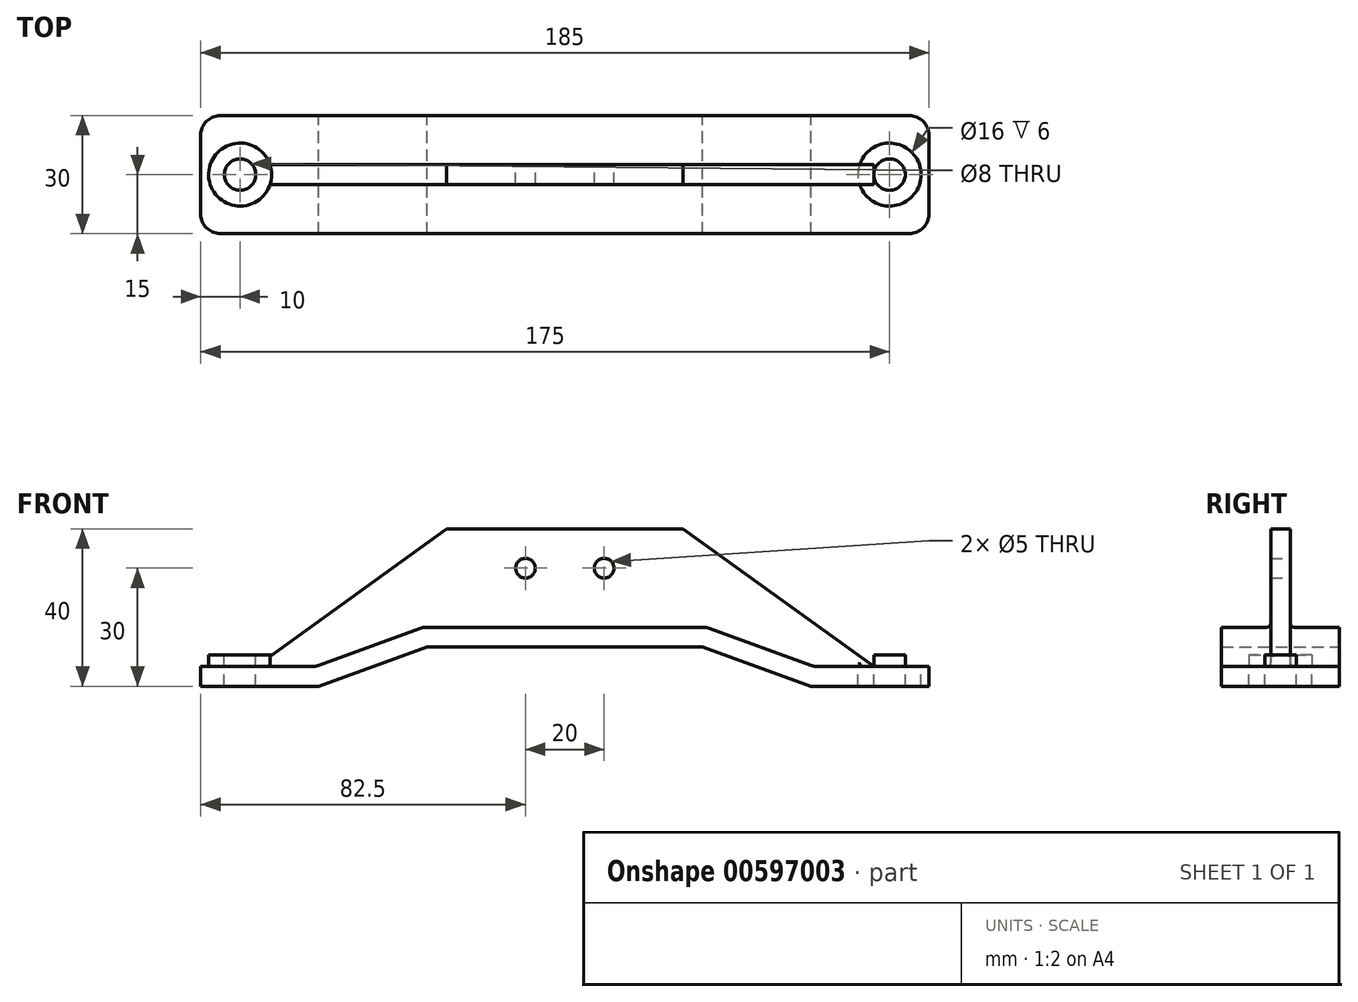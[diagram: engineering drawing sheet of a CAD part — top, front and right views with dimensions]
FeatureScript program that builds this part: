
annotation { "Feature Type Name" : "Feature", "Feature Type Description" : "" }
export const myFeature = defineFeature(function(context is Context, id is Id, definition is map)
    precondition{}
    {
        {
            var Q0;
            Q0=qCreatedBy(makeId("Front.planeOp"),FACE);
            var sketch = newSketch(context, id + "F0", { "sketchPlane" : qUnion([Q0])});
            skLineSegment(sketch, "E0", {"start": v(0, 0) * mm, "end": v(-35.03, 0) * mm});
            skLineSegment(sketch, "E1", {"start": v(-35.03, 0) * mm, "end": v(-62.5, -10) * mm});
            skLineSegment(sketch, "E2", {"start": v(-62.5, -10) * mm, "end": v(-92.5, -10) * mm});
            skLineSegment(sketch, "E3.MirrorCS", {"start": v(0, 0) * mm, "end": v(35.03, 0) * mm});
            skLineSegment(sketch, "E4.MirrorCS", {"start": v(35.03, 0) * mm, "end": v(62.5, -10) * mm});
            skLineSegment(sketch, "E5.MirrorCS", {"start": v(62.5, -10) * mm, "end": v(92.5, -10) * mm});
            skLineSegment(sketch, "E6", {"start": v(-62.5, -10) * mm, "end": v(0, -10) * mm, "construction": true});
            skLineSegment(sketch, "E7.0", {"start": v(-63.38, -5) * mm, "end": v(-92.5, -5) * mm});
            skLineSegment(sketch, "E7.1", {"start": v(-35.9, 5) * mm, "end": v(-63.38, -5) * mm});
            skLineSegment(sketch, "E7.2", {"start": v(63.38, -5) * mm, "end": v(92.5, -5) * mm});
            skLineSegment(sketch, "E7.3", {"start": v(35.9, 5) * mm, "end": v(63.38, -5) * mm});
            skLineSegment(sketch, "E7.4", {"start": v(0, 5) * mm, "end": v(35.9, 5) * mm});
            skLineSegment(sketch, "E7.5", {"start": v(0, 5) * mm, "end": v(-35.9, 5) * mm});
            skLineSegment(sketch, "E8", {"start": v(-92.5, -5) * mm, "end": v(-92.5, -10) * mm});
            skLineSegment(sketch, "E9", {"start": v(92.5, -5) * mm, "end": v(92.5, -10) * mm});
            skLineSegment(sketch, "E10", {"start": v(-78.5, -5) * mm, "end": v(-30, 30) * mm});
            skLineSegment(sketch, "E11", {"start": v(-30, 30) * mm, "end": v(0, 30) * mm});
            skLineSegment(sketch, "E12.MirrorCS", {"start": v(30, 30) * mm, "end": v(0, 30) * mm});
            skLineSegment(sketch, "E13.MirrorCS", {"start": v(78.5, -5) * mm, "end": v(30, 30) * mm});
            skCircle(sketch, "E14", {"center": v(-10, 20) * mm, "radius": 2.5 * mm});
            skCircle(sketch, "E15.MirrorC", {"center": v(10, 20) * mm, "radius": 2.5 * mm});
            skSolve(sketch);
        }
        {
            var Q0;
            Q0=makeQuery(id+"F0.imprint","IMPRINT",FACE,{"disambiguationData":[TD([[makeQuery(id+"F0.imprint","IMPRINT",EDGE,{"derivedFrom":sQuery(id+"F0.wireOp",EDGE,"E0")}),-1.0]])]});
            extrude(context, id + "F1", {"entities" : qUnion([Q0]), "endBound" : BoundingType.SYMMETRIC, "depth" : 30 * mm, "offsetDistance" : 25 * mm});
        }
        {
            var Q0;
            Q0=makeQuery(id+"F1.opExtrude","SWEPT_FACE",FACE,{"disambiguationData":[OSD([sQuery(id+"F0.wireOp",EDGE,"E7.0")])]});
            var sketch = newSketch(context, id + "F2", { "sketchPlane" : qUnion([Q0])});
            skCircle(sketch, "E16", {"center": v(-82.5, 0) * mm, "radius": 4 * mm});
            skLineSegment(sketch, "E17", {"start": v(-92.5, 0) * mm, "end": v(-82.5, 0) * mm, "construction": true});
            skPoint(sketch, "E17.endSnap0", {"position": v(-92.5, 0) * mm});
            skCircle(sketch, "E18.MirrorC", {"center": v(82.5, 0) * mm, "radius": 4 * mm});
            skCircle(sketch, "E19.0", {"center": v(-82.5, 0) * mm, "radius": 8 * mm});
            skCircle(sketch, "E20.MirrorC", {"center": v(82.5, 0) * mm, "radius": 8 * mm});
            skSolve(sketch);
        }
        {
            var Q0;
            Q0 = qSketchRegion(id + "F0", true);
            extrude(context, id + "F3", {"entities" : qUnion([Q0]), "operationType" : NewBodyOperationType.ADD, "endBound" : BoundingType.SYMMETRIC, "depth" : 5 * mm, "offsetDistance" : 25 * mm});
        }
        {
            var Q0;
            Q0=makeQuery(id+"F2.imprint","IMPRINT",FACE,{"disambiguationData":[TD([[makeQuery(id+"F2.imprint","IMPRINT",EDGE,{"derivedFrom":sQuery(id+"F2.wireOp",EDGE,"E16")}),1.0]])]});
            var Q1;
            Q1=makeQuery(id+"F2.imprint","IMPRINT",FACE,{"disambiguationData":[TD([[makeQuery(id+"F2.imprint","IMPRINT",EDGE,{"derivedFrom":sQuery(id+"F2.wireOp",EDGE,"E18.MirrorC")}),-1.0]])]});
            extrude(context, id + "F4", {"entities" : qUnion([Q0, Q1]), "operationType" : NewBodyOperationType.REMOVE, "endBound" : BoundingType.THROUGH_ALL, "oppositeDirection" : true, "depth" : 25 * mm, "offsetDistance" : 25 * mm});
        }
        {
            var Q0;
            {var subQ0=sQuery(id+"F0.wireOp",EDGE,"E9");var subQ1=sQuery(id+"F0.wireOp",EDGE,"E8");var subQ2=sQuery(id+"F0.wireOp",EDGE,"E7.2");var subQ3=sQuery(id+"F0.wireOp",EDGE,"E7.1");var subQ4=sQuery(id+"F0.wireOp",EDGE,"E7.0");var subQ5=sQuery(id+"F0.wireOp",EDGE,"E5.MirrorCS");var subQ6=sQuery(id+"F0.wireOp",EDGE,"E4.MirrorCS");var subQ7=sQuery(id+"F0.wireOp",EDGE,"E3.MirrorCS");var subQ8=sQuery(id+"F0.wireOp",EDGE,"E2");var subQ9=sQuery(id+"F0.wireOp",EDGE,"E1");var subQ10=sQuery(id+"F0.wireOp",EDGE,"E0");Q0=makeQuery(id+"F3.boolean.opBoolean","SPLIT",EDGE,{"disambiguationData":[TD([makeQuery(id+"F1.opExtrude","CAP_FACE",FACE,{"disambiguationData":[OSD([subQ10,subQ9,subQ8,subQ7,subQ6,subQ5,subQ4,subQ3,subQ2,sQuery(id+"F0.wireOp",EDGE,"E7.3"),sQuery(id+"F0.wireOp",EDGE,"E7.4"),sQuery(id+"F0.wireOp",EDGE,"E7.5"),subQ1,subQ0])],"isStart":false})])],"derivedFrom":makeQuery(id+"F1.opExtrude","SWEPT_EDGE",EDGE,{"disambiguationData":[OSD([subQ4,subQ3])]})});}
            var Q1;
            {var subQ0=sQuery(id+"F0.wireOp",EDGE,"E9");var subQ1=sQuery(id+"F0.wireOp",EDGE,"E8");var subQ2=sQuery(id+"F0.wireOp",EDGE,"E7.2");var subQ3=sQuery(id+"F0.wireOp",EDGE,"E7.1");var subQ4=sQuery(id+"F0.wireOp",EDGE,"E7.0");var subQ5=sQuery(id+"F0.wireOp",EDGE,"E5.MirrorCS");var subQ6=sQuery(id+"F0.wireOp",EDGE,"E4.MirrorCS");var subQ7=sQuery(id+"F0.wireOp",EDGE,"E3.MirrorCS");var subQ8=sQuery(id+"F0.wireOp",EDGE,"E2");var subQ9=sQuery(id+"F0.wireOp",EDGE,"E1");var subQ10=sQuery(id+"F0.wireOp",EDGE,"E0");Q1=makeQuery(id+"F3.boolean.opBoolean","SPLIT",EDGE,{"disambiguationData":[TD([makeQuery(id+"F1.opExtrude","CAP_FACE",FACE,{"disambiguationData":[OSD([subQ10,subQ9,subQ8,subQ7,subQ6,subQ5,subQ4,subQ3,subQ2,sQuery(id+"F0.wireOp",EDGE,"E7.3"),sQuery(id+"F0.wireOp",EDGE,"E7.4"),sQuery(id+"F0.wireOp",EDGE,"E7.5"),subQ1,subQ0])],"isStart":true})])],"derivedFrom":makeQuery(id+"F1.opExtrude","SWEPT_EDGE",EDGE,{"disambiguationData":[OSD([subQ4,subQ3])]})});}
            var Q2;
            {var subQ0=sQuery(id+"F0.wireOp",EDGE,"E9");var subQ1=sQuery(id+"F0.wireOp",EDGE,"E8");var subQ2=sQuery(id+"F0.wireOp",EDGE,"E7.5");var subQ3=sQuery(id+"F0.wireOp",EDGE,"E7.4");var subQ4=sQuery(id+"F0.wireOp",EDGE,"E7.2");var subQ5=sQuery(id+"F0.wireOp",EDGE,"E7.1");var subQ6=sQuery(id+"F0.wireOp",EDGE,"E7.0");var subQ7=sQuery(id+"F0.wireOp",EDGE,"E5.MirrorCS");var subQ8=sQuery(id+"F0.wireOp",EDGE,"E4.MirrorCS");var subQ9=sQuery(id+"F0.wireOp",EDGE,"E3.MirrorCS");var subQ10=sQuery(id+"F0.wireOp",EDGE,"E2");var subQ11=sQuery(id+"F0.wireOp",EDGE,"E1");var subQ12=sQuery(id+"F0.wireOp",EDGE,"E0");Q2=makeQuery(id+"F3.boolean.opBoolean","SPLIT",EDGE,{"disambiguationData":[TD([makeQuery(id+"F1.opExtrude","CAP_FACE",FACE,{"disambiguationData":[OSD([subQ12,subQ11,subQ10,subQ9,subQ8,subQ7,subQ6,subQ5,subQ4,sQuery(id+"F0.wireOp",EDGE,"E7.3"),subQ3,subQ2,subQ1,subQ0])],"isStart":false})])],"derivedFrom":makeQuery(id+"F1.opExtrude","SWEPT_EDGE",EDGE,{"disambiguationData":[OSD([subQ5,subQ2])]})});}
            var Q3;
            {var subQ0=sQuery(id+"F0.wireOp",EDGE,"E9");var subQ1=sQuery(id+"F0.wireOp",EDGE,"E8");var subQ2=sQuery(id+"F0.wireOp",EDGE,"E7.5");var subQ3=sQuery(id+"F0.wireOp",EDGE,"E7.4");var subQ4=sQuery(id+"F0.wireOp",EDGE,"E7.2");var subQ5=sQuery(id+"F0.wireOp",EDGE,"E7.1");var subQ6=sQuery(id+"F0.wireOp",EDGE,"E7.0");var subQ7=sQuery(id+"F0.wireOp",EDGE,"E5.MirrorCS");var subQ8=sQuery(id+"F0.wireOp",EDGE,"E4.MirrorCS");var subQ9=sQuery(id+"F0.wireOp",EDGE,"E3.MirrorCS");var subQ10=sQuery(id+"F0.wireOp",EDGE,"E2");var subQ11=sQuery(id+"F0.wireOp",EDGE,"E1");var subQ12=sQuery(id+"F0.wireOp",EDGE,"E0");Q3=makeQuery(id+"F3.boolean.opBoolean","SPLIT",EDGE,{"disambiguationData":[TD([makeQuery(id+"F1.opExtrude","CAP_FACE",FACE,{"disambiguationData":[OSD([subQ12,subQ11,subQ10,subQ9,subQ8,subQ7,subQ6,subQ5,subQ4,sQuery(id+"F0.wireOp",EDGE,"E7.3"),subQ3,subQ2,subQ1,subQ0])],"isStart":true})])],"derivedFrom":makeQuery(id+"F1.opExtrude","SWEPT_EDGE",EDGE,{"disambiguationData":[OSD([subQ5,subQ2])]})});}
            var Q4;
            {var subQ0=sQuery(id+"F0.wireOp",EDGE,"E9");var subQ1=sQuery(id+"F0.wireOp",EDGE,"E8");var subQ2=sQuery(id+"F0.wireOp",EDGE,"E7.3");var subQ3=sQuery(id+"F0.wireOp",EDGE,"E7.2");var subQ4=sQuery(id+"F0.wireOp",EDGE,"E7.0");var subQ5=sQuery(id+"F0.wireOp",EDGE,"E5.MirrorCS");var subQ6=sQuery(id+"F0.wireOp",EDGE,"E4.MirrorCS");var subQ7=sQuery(id+"F0.wireOp",EDGE,"E3.MirrorCS");var subQ8=sQuery(id+"F0.wireOp",EDGE,"E2");var subQ9=sQuery(id+"F0.wireOp",EDGE,"E1");var subQ10=sQuery(id+"F0.wireOp",EDGE,"E0");Q4=makeQuery(id+"F3.boolean.opBoolean","SPLIT",EDGE,{"disambiguationData":[TD([makeQuery(id+"F1.opExtrude","CAP_FACE",FACE,{"disambiguationData":[OSD([subQ10,subQ9,subQ8,subQ7,subQ6,subQ5,subQ4,sQuery(id+"F0.wireOp",EDGE,"E7.1"),subQ3,subQ2,sQuery(id+"F0.wireOp",EDGE,"E7.4"),sQuery(id+"F0.wireOp",EDGE,"E7.5"),subQ1,subQ0])],"isStart":true})])],"derivedFrom":makeQuery(id+"F1.opExtrude","SWEPT_EDGE",EDGE,{"disambiguationData":[OSD([subQ3,subQ2])]})});}
            var Q5;
            {var subQ0=sQuery(id+"F0.wireOp",EDGE,"E9");var subQ1=sQuery(id+"F0.wireOp",EDGE,"E8");var subQ2=sQuery(id+"F0.wireOp",EDGE,"E7.3");var subQ3=sQuery(id+"F0.wireOp",EDGE,"E7.2");var subQ4=sQuery(id+"F0.wireOp",EDGE,"E7.0");var subQ5=sQuery(id+"F0.wireOp",EDGE,"E5.MirrorCS");var subQ6=sQuery(id+"F0.wireOp",EDGE,"E4.MirrorCS");var subQ7=sQuery(id+"F0.wireOp",EDGE,"E3.MirrorCS");var subQ8=sQuery(id+"F0.wireOp",EDGE,"E2");var subQ9=sQuery(id+"F0.wireOp",EDGE,"E1");var subQ10=sQuery(id+"F0.wireOp",EDGE,"E0");Q5=makeQuery(id+"F3.boolean.opBoolean","SPLIT",EDGE,{"disambiguationData":[TD([makeQuery(id+"F1.opExtrude","CAP_FACE",FACE,{"disambiguationData":[OSD([subQ10,subQ9,subQ8,subQ7,subQ6,subQ5,subQ4,sQuery(id+"F0.wireOp",EDGE,"E7.1"),subQ3,subQ2,sQuery(id+"F0.wireOp",EDGE,"E7.4"),sQuery(id+"F0.wireOp",EDGE,"E7.5"),subQ1,subQ0])],"isStart":false})])],"derivedFrom":makeQuery(id+"F1.opExtrude","SWEPT_EDGE",EDGE,{"disambiguationData":[OSD([subQ3,subQ2])]})});}
            var Q6;
            {var subQ0=sQuery(id+"F0.wireOp",EDGE,"E9");var subQ1=sQuery(id+"F0.wireOp",EDGE,"E8");var subQ2=sQuery(id+"F0.wireOp",EDGE,"E7.5");var subQ3=sQuery(id+"F0.wireOp",EDGE,"E7.4");var subQ4=sQuery(id+"F0.wireOp",EDGE,"E7.3");var subQ5=sQuery(id+"F0.wireOp",EDGE,"E7.2");var subQ6=sQuery(id+"F0.wireOp",EDGE,"E7.0");var subQ7=sQuery(id+"F0.wireOp",EDGE,"E5.MirrorCS");var subQ8=sQuery(id+"F0.wireOp",EDGE,"E4.MirrorCS");var subQ9=sQuery(id+"F0.wireOp",EDGE,"E3.MirrorCS");var subQ10=sQuery(id+"F0.wireOp",EDGE,"E2");var subQ11=sQuery(id+"F0.wireOp",EDGE,"E1");var subQ12=sQuery(id+"F0.wireOp",EDGE,"E0");Q6=makeQuery(id+"F3.boolean.opBoolean","SPLIT",EDGE,{"disambiguationData":[TD([makeQuery(id+"F1.opExtrude","CAP_FACE",FACE,{"disambiguationData":[OSD([subQ12,subQ11,subQ10,subQ9,subQ8,subQ7,subQ6,sQuery(id+"F0.wireOp",EDGE,"E7.1"),subQ5,subQ4,subQ3,subQ2,subQ1,subQ0])],"isStart":false})])],"derivedFrom":makeQuery(id+"F1.opExtrude","SWEPT_EDGE",EDGE,{"disambiguationData":[OSD([subQ4,subQ3])]})});}
            var Q7;
            {var subQ0=sQuery(id+"F0.wireOp",EDGE,"E9");var subQ1=sQuery(id+"F0.wireOp",EDGE,"E8");var subQ2=sQuery(id+"F0.wireOp",EDGE,"E7.5");var subQ3=sQuery(id+"F0.wireOp",EDGE,"E7.4");var subQ4=sQuery(id+"F0.wireOp",EDGE,"E7.3");var subQ5=sQuery(id+"F0.wireOp",EDGE,"E7.2");var subQ6=sQuery(id+"F0.wireOp",EDGE,"E7.0");var subQ7=sQuery(id+"F0.wireOp",EDGE,"E5.MirrorCS");var subQ8=sQuery(id+"F0.wireOp",EDGE,"E4.MirrorCS");var subQ9=sQuery(id+"F0.wireOp",EDGE,"E3.MirrorCS");var subQ10=sQuery(id+"F0.wireOp",EDGE,"E2");var subQ11=sQuery(id+"F0.wireOp",EDGE,"E1");var subQ12=sQuery(id+"F0.wireOp",EDGE,"E0");Q7=makeQuery(id+"F3.boolean.opBoolean","SPLIT",EDGE,{"disambiguationData":[TD([makeQuery(id+"F1.opExtrude","CAP_FACE",FACE,{"disambiguationData":[OSD([subQ12,subQ11,subQ10,subQ9,subQ8,subQ7,subQ6,sQuery(id+"F0.wireOp",EDGE,"E7.1"),subQ5,subQ4,subQ3,subQ2,subQ1,subQ0])],"isStart":true})])],"derivedFrom":makeQuery(id+"F1.opExtrude","SWEPT_EDGE",EDGE,{"disambiguationData":[OSD([subQ4,subQ3])]})});}
            fillet(context, id + "F5", {"entities" : qUnion([Q0, Q1, Q2, Q3, Q4, Q5, Q6, Q7]), "radius" : 5 * mm, "tangentPropagation" : true, "allowEdgeOverflow" : false});
        }
        {
            var Q0;
            Q0=makeQuery(id+"F3.boolean.opBoolean","INTERSECT",EDGE,{"derivedFrom":[makeQuery(id+"F1.opExtrude","SWEPT_FACE",FACE,{"disambiguationData":[OSD([sQuery(id+"F0.wireOp",EDGE,"E7.4"),sQuery(id+"F0.wireOp",EDGE,"E7.5")])]}),makeQuery(id+"F3.opExtrude","CAP_FACE",FACE,{"disambiguationData":[OSD([sQuery(id+"F0.wireOp",EDGE,"E0"),sQuery(id+"F0.wireOp",EDGE,"E1"),sQuery(id+"F0.wireOp",EDGE,"E2"),sQuery(id+"F0.wireOp",EDGE,"E3.MirrorCS"),sQuery(id+"F0.wireOp",EDGE,"E4.MirrorCS"),sQuery(id+"F0.wireOp",EDGE,"E5.MirrorCS"),sQuery(id+"F0.wireOp",EDGE,"E7.0"),sQuery(id+"F0.wireOp",EDGE,"E7.2"),sQuery(id+"F0.wireOp",EDGE,"E8"),sQuery(id+"F0.wireOp",EDGE,"E9"),sQuery(id+"F0.wireOp",EDGE,"E10"),sQuery(id+"F0.wireOp",EDGE,"E11"),sQuery(id+"F0.wireOp",EDGE,"E12.MirrorCS"),sQuery(id+"F0.wireOp",EDGE,"E13.MirrorCS")])],"isStart":false})]});
            var Q1;
            Q1=makeQuery(id+"F3.boolean.opBoolean","INTERSECT",EDGE,{"derivedFrom":[makeQuery(id+"F1.opExtrude","SWEPT_FACE",FACE,{"disambiguationData":[OSD([sQuery(id+"F0.wireOp",EDGE,"E7.4"),sQuery(id+"F0.wireOp",EDGE,"E7.5")])]}),makeQuery(id+"F3.opExtrude","CAP_FACE",FACE,{"disambiguationData":[OSD([sQuery(id+"F0.wireOp",EDGE,"E0"),sQuery(id+"F0.wireOp",EDGE,"E1"),sQuery(id+"F0.wireOp",EDGE,"E2"),sQuery(id+"F0.wireOp",EDGE,"E3.MirrorCS"),sQuery(id+"F0.wireOp",EDGE,"E4.MirrorCS"),sQuery(id+"F0.wireOp",EDGE,"E5.MirrorCS"),sQuery(id+"F0.wireOp",EDGE,"E7.0"),sQuery(id+"F0.wireOp",EDGE,"E7.2"),sQuery(id+"F0.wireOp",EDGE,"E8"),sQuery(id+"F0.wireOp",EDGE,"E9"),sQuery(id+"F0.wireOp",EDGE,"E10"),sQuery(id+"F0.wireOp",EDGE,"E11"),sQuery(id+"F0.wireOp",EDGE,"E12.MirrorCS"),sQuery(id+"F0.wireOp",EDGE,"E13.MirrorCS")])],"isStart":true})]});
            fillet(context, id + "F6", {"entities" : qUnion([Q0, Q1]), "radius" : 1 * mm, "tangentPropagation" : true, "allowEdgeOverflow" : false});
        }
        {
            var Q0;
            Q0=makeQuery(id+"F1.opExtrude","CAP_EDGE",EDGE,{"disambiguationData":[OSD([sQuery(id+"F0.wireOp",EDGE,"E8")])],"isStart":false});
            var Q1;
            Q1=makeQuery(id+"F1.opExtrude","CAP_EDGE",EDGE,{"disambiguationData":[OSD([sQuery(id+"F0.wireOp",EDGE,"E9")])],"isStart":false});
            var Q2;
            Q2=makeQuery(id+"F1.opExtrude","CAP_EDGE",EDGE,{"disambiguationData":[OSD([sQuery(id+"F0.wireOp",EDGE,"E9")])],"isStart":true});
            var Q3;
            Q3=makeQuery(id+"F1.opExtrude","CAP_EDGE",EDGE,{"disambiguationData":[OSD([sQuery(id+"F0.wireOp",EDGE,"E8")])],"isStart":true});
            fillet(context, id + "F7", {"entities" : qUnion([Q0, Q1, Q2, Q3]), "radius" : 5 * mm, "tangentPropagation" : true, "allowEdgeOverflow" : false});
        }
        {
            var Q0;
            Q0=makeQuery(id+"F2.imprint","IMPRINT",FACE,{"disambiguationData":[TD([[makeQuery(id+"F2.imprint","IMPRINT",EDGE,{"derivedFrom":sQuery(id+"F2.wireOp",EDGE,"E16")}),-1.0]])]});
            var Q1;
            Q1=makeQuery(id+"F2.imprint","IMPRINT",FACE,{"disambiguationData":[TD([[makeQuery(id+"F2.imprint","IMPRINT",EDGE,{"derivedFrom":sQuery(id+"F2.wireOp",EDGE,"E18.MirrorC")}),1.0]])]});
            extrude(context, id + "F8", {"entities" : qUnion([Q0, Q1]), "operationType" : NewBodyOperationType.ADD, "depth" : 3 * mm, "offsetDistance" : 25 * mm});
        }
    });
